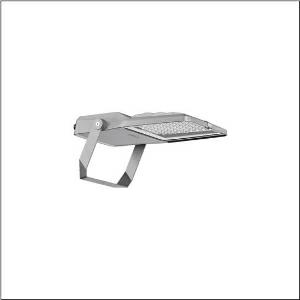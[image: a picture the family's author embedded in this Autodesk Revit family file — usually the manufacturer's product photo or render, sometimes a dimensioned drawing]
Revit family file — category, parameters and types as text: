
# Revit family: floodlight_fl_21_iq_mini___rs12_5xa7772b1b1a_07b1
name_source: partatom
category: Lighting Fixtures
units: mm (PartAtom-declared; Revit-internal decimal feet)

## family parameters
Cut with Voids When Loaded = No
Host = Face
Light Source = No
Part Type = Normal
Room Calculation Point = No
Round Connector Dimension = Use Diameter
Shared = No

## types (1)
- --- (1 x LED, 5230 lm, 45.5 W, 2200K)
    Apparent Load = 46 VA
    CIE Flux Codes = 79 92 99 100 100
    Color Rendering = 70
    Color Temperature = 2200K
    Default Elevation = 1800 mm
    Description = Floodlight FL 21 iQ mini, floodlight, primary light control with lens, of PMMA, primary optical cover: protective disc, of toughened safety glass, transparent, light distribution: RS12, light emission: direct distribution, installation type: surface-mounted, LED, High Power LED, rated luminous flux: 5.230lm, luminous efficacy: 115lm/W, light colour: 722, colour temperature: 2200K, control gear: iQ Street-Remote/DALI, control: Street-Remote, Auto-Match, Temp-Guard, Night-Set, Smart-Wire, Desk-Remote (wireless, voltage-free reading and setting of iQ features in the workshop via application-optimized NFC function/RFID function), optimised constant luminous flux control (CLO 2.0), with terminal, 6-pole, mains connection: 220..240V, AC, 50/60Hz, start of lifetime: 46W, end of service life: 48W, reduction: 21W, luminaire housing, of diecast aluminium, powder-coated, Siteco® metallic grey (DB 702S), corrosivity category C5 mid according to DIN EN ISO 12944, suitable for swimming pools, chlorine-resistant, sealing non-destructively replaceable, mounting bracket, of steel, galvanised, powder-coated, Siteco® metallic grey (DB 702S), protection rating (complete): IP66, insulation class (complete): insulation class II (safety insulation), certification: CE, ENEC, VDE, protection symbol: D, impact resistance: IK08, permissible operating ambient temperature: -40..+40°C, permissible operating ambient temperature for outdoor applications: -40..+50°C, standard: DIN EN 12944, LABS conformity tested according to VDMA 24364:2018-05, packaging unit: 1 piece

Light Distribution: RS12
    Height = 70 mm
    Lamp = 1 x LED
    Lamp Light Flux = 5230 lm
    Lamp Power = 45.5 W
    Lamp count = 1
    Length = 485 mm
    Luminous efficacy = 115 lm/W
    Manufacturer = Siteco
    ModVariant = No
    Model = 5XA7772B1B1A
    Number of Poles = 1
    OnlyDefault = Yes
    Power Factor = 1
    Product Name = Floodlight FL 21 iQ mini | RS12
    Product group = floodlight | pylon annexe
    ProductGroupID = 6200
    Protection Class = Protection class II
    Protection Degree = IP 66
    RLX_Detail_Level = 1
    RLX_Emergency_Light_Flux = 0 lm
    RLX_Emergency_Type = 0
    RLX_Emergency_Type_DB = No
    RlxData = <blob elided: 90925 chars, md5=35e59c14>
    Socket = socket
    Standby Power = 0 W
    System Light Flux = 5230 lm
    System Power = 46 W
    Type Comments = factory setting: luminous flux: 100 % | dim-lin: 254 | 463 mA
    Type Image = l_1006845.jpg
    URL = http://relux.com
    VarID = @adj_167924
    Voltage = 0 V
    Weight = 0.00 kg
    Width = 337 mm

## geometry (parser evidence)
native form markers: Blend x4, Sweep x12
no freeform markers — native parametric forms only
